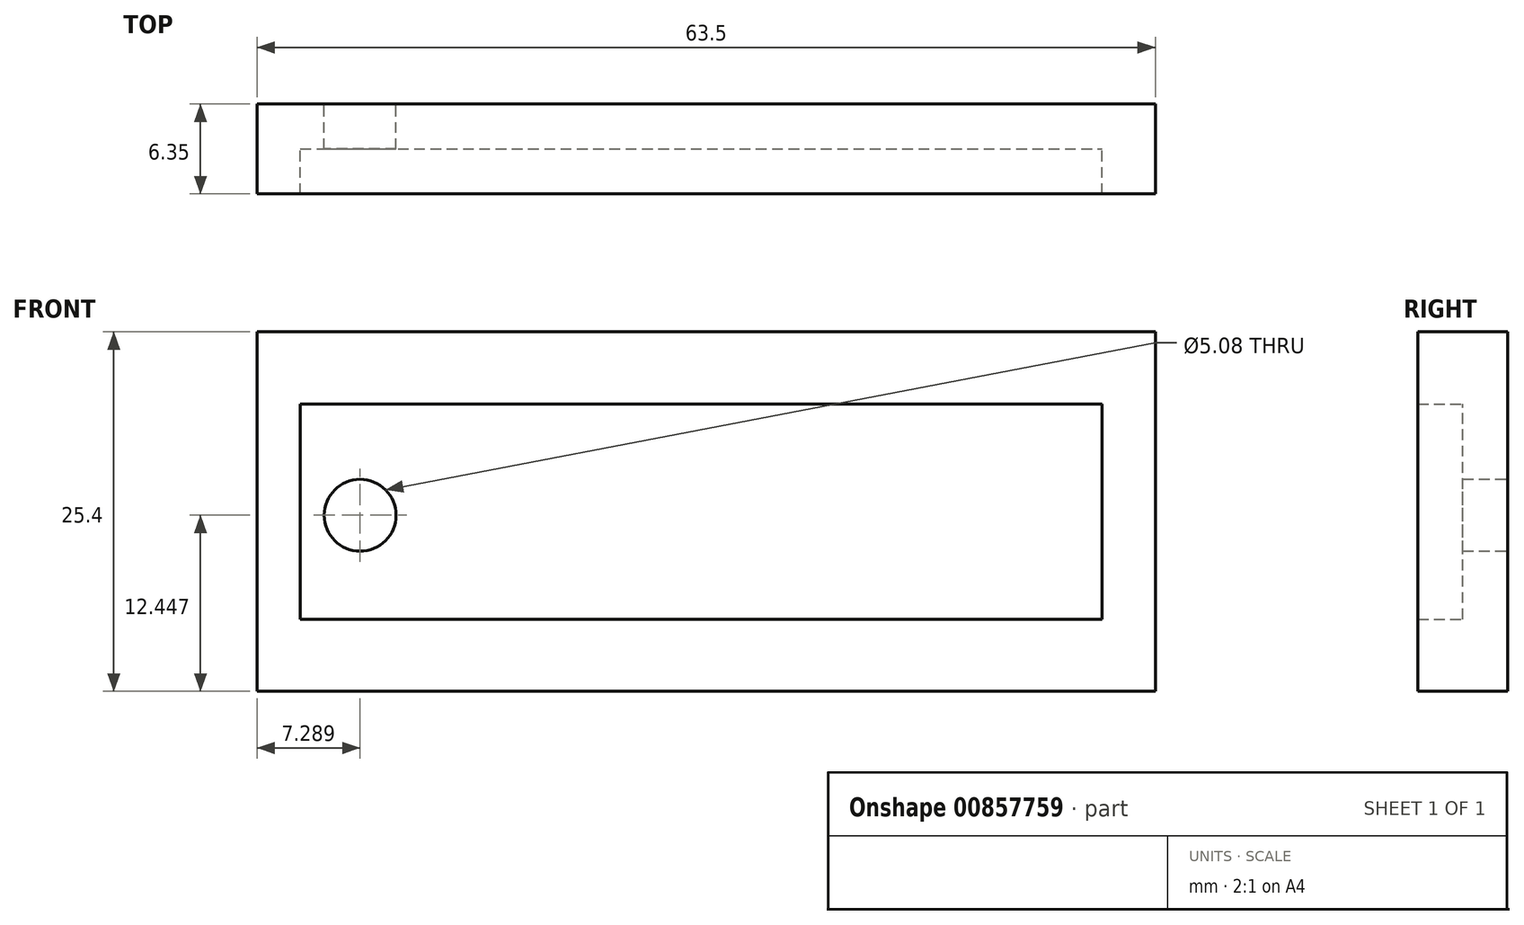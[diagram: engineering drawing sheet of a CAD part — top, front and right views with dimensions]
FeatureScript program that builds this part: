
annotation { "Feature Type Name" : "Feature", "Feature Type Description" : "" }
export const myFeature = defineFeature(function(context is Context, id is Id, definition is map)
    precondition{}
    {
        {
            var Q0;
            Q0=qCreatedBy(makeId("Front.planeOp"),FACE);
            var sketch = newSketch(context, id + "F0", { "sketchPlane" : qUnion([Q0])});
            skLineSegment(sketch, "E0.bottom", {"start": v(0, 0) * mm, "end": v(63.5, 0) * mm});
            skLineSegment(sketch, "E0.top", {"start": v(0, 25.4) * mm, "end": v(63.5, 25.4) * mm});
            skLineSegment(sketch, "E0.left", {"start": v(0, 0) * mm, "end": v(0, 25.4) * mm});
            skLineSegment(sketch, "E0.right", {"start": v(63.5, 0) * mm, "end": v(63.5, 25.4) * mm});
            skLineSegment(sketch, "E1.bottom", {"start": v(3.07, 25.4) * mm, "end": v(3.07, 25.4) * mm});
            skLineSegment(sketch, "E1.top", {"start": v(3.07, 5.11) * mm, "end": v(3.07, 5.11) * mm});
            skLineSegment(sketch, "E2.bottom", {"start": v(3.07, 5.11) * mm, "end": v(59.72, 5.11) * mm});
            skLineSegment(sketch, "E2.top", {"start": v(3.07, 20.3) * mm, "end": v(59.72, 20.3) * mm});
            skLineSegment(sketch, "E2.left", {"start": v(3.07, 5.11) * mm, "end": v(3.07, 20.3) * mm});
            skLineSegment(sketch, "E2.right", {"start": v(59.72, 5.11) * mm, "end": v(59.72, 20.3) * mm});
            skSolve(sketch);
        }
        {
            var Q0;
            Q0 = qSketchRegion(id + "F0", true);
            extrude(context, id + "F1", {"entities" : qUnion([Q0]), "depth" : 6.35 * mm, "offsetDistance" : 25.4 * mm});
        }
        {
            var Q0;
            Q0=makeQuery(id+"F0.imprint","IMPRINT",FACE,{"disambiguationData":[TD([[makeQuery(id+"F0.imprint","IMPRINT",EDGE,{"derivedFrom":sQuery(id+"F0.wireOp",EDGE,"E2.bottom")}),1.0]])]});
            extrude(context, id + "F2", {"entities" : qUnion([Q0]), "operationType" : NewBodyOperationType.ADD, "depth" : 3.17 * mm, "offsetDistance" : 25.4 * mm});
        }
        {
            var Q0;
            Q0=qCreatedBy(makeId("Front.planeOp"),FACE);
            var sketch = newSketch(context, id + "F3", { "sketchPlane" : qUnion([Q0])});
            skCircle(sketch, "E3", {"center": v(7.29, 12.45) * mm, "radius": 2.54 * mm});
            skSolve(sketch);
        }
        {
            var Q0;
            Q0 = qSketchRegion(id + "F3", true);
            extrude(context, id + "F4", {"entities" : qUnion([Q0]), "operationType" : NewBodyOperationType.REMOVE, "depth" : 25.4 * mm, "offsetDistance" : 25.4 * mm});
        }
    });
